# Revit family: SUPER
name_source: partatom
category: Plumbing Fixtures
units: mm (PartAtom-declared; Revit-internal decimal feet)

## family parameters
Always vertical = Yes
Cut with Voids When Loaded = No
OmniClass Number = 23.45.00.00
OmniClass Title = Sanitary, Laundry, and Cleaning Equipment
Part Type = Normal
Room Calculation Point = No
Round Connector Dimension = Use Diameter
Shared = No
Work Plane-Based = No

## types (6) — shared parameters
Base material = Default
Manufacturer = MIFAB
Material = Polyethylene, High Density
URL = www.mifab.com

## per-type parameters (varying)
| type | Depth | Description | H | H1 | Model | RP Left | RP Right | a |
| SUPER-500 | 18" | 500gallon Liquid Hold Cap. Grease Int. | 61 1/2" | 38 1/2" | SM-MI-G-PL-500 | 26 1/4" | 24 1/4" | 8" |
| SUPER-750 | 19" | 750gallon Liquid Hold Cap. Grease Int. | 70 1/8" | 46 1/2" | SM-MI-G-PL-750 | 34 1/4" | 32 1/4" | 13" |
| SUPER-1000 | 21" | 1000gallon Liquid Hold Cap. Grease Int. | 80 1/2" | 57 1/2" | SM-MI-G-PL-1000 | 45 1/4" | 43 1/4" | 0" |
| SUPER-1300 | 21" | 1300gallon Liquid Hold Cap. Grease Int. | 91 1/2" | 68 1/2" | SM-MI-G-PL-1300 | 56 1/4" | 54 1/4" | 0" |
| SUPER-1500 | 21" | 1500gallon Liquid Hold Cap. Grease Int. | 99 1/4" | 76 1/4" | SM-MI-G-PL-1500 | 64" | 62" | 0" |
| SUPER-1250 | 21" | 1250gallon Liquid Hold Cap. Grease Int. | 91 1/2" | 68 1/2" | SM-MI-G-PL-1250 | 56 1/4" | 54 1/4" | 0" |

## geometry (parser evidence)
native form markers: Sweep x3
no freeform markers — native parametric forms only
